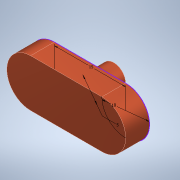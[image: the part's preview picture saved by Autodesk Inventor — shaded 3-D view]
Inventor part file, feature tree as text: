
AUTODESK INVENTOR PART (.ipt)
format: ipt  version: 2022 (Build 260153000, 153)  size: 110,080 bytes
history: native  units: mm
features: extrude x2, sketch x1
ambient origin geometry x8: Origin, YZ Plane, XZ Plane, XY Plane, X Axis, Y Axis, Z Axis, Center Point
bodies: Body1 (feature_tree)
feature tree (3):
  sketch  "Sketch1"  dims[d0=10.0mm d1=5.0mm d7=5.0mm d8=0.0mm d9=5.0mm d10=0.0mm d11=15.0mm]
  extrude  "Extrusion3"  Depth=5.0mm
  extrude  "Extrusion4"  Depth=5.0mm TaperAngle=0.0deg
